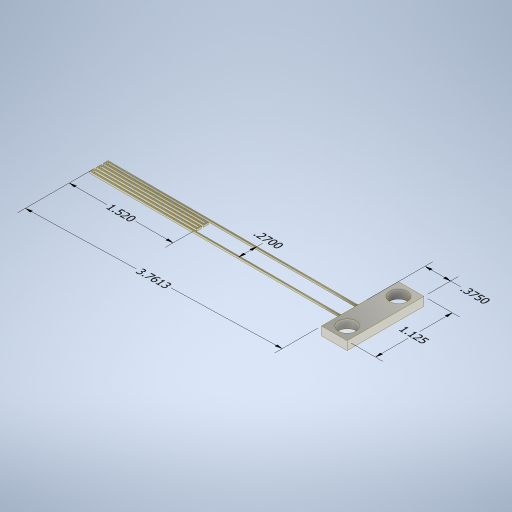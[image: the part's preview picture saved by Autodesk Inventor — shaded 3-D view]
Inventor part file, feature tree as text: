
AUTODESK INVENTOR PART (.ipt)
format: ipt  version: 2024.2 (Build 282272000, 272)  size: 348,160 bytes
history: native  units: in
note: dims shown in document units (in); Inventor stores cm internally (conversion verified against a paired STEP export)
features: other x6, sketch x4, plane x2, extrude x2, fillet x2, sweep x1
ambient origin geometry x8: Origin, YZ Plane, XZ Plane, XY Plane, X Axis, Y Axis, Z Axis, Center Point
bodies: Solid1 (feature_tree)
feature tree (17):
  other  "Annotations"
  sweep  "Sweep1"
  plane  "Work Plane1"
  plane  "Work Plane2"
  extrude  "Extrusion4"  Depth=0.05in
  fillet  "Fillet1"  Radius=0.05in
  extrude  "Extrusion5"  TaperAngle=0.0deg  [1 undecoded]
  fillet  "Fillet2"  Radius=0.05in
  sketch  "Sketch1"  dims[d0=3.75in d1=0.05in]
  sketch  "Sketch2"  dims[d2=1.5in d3=0.05in d4=0.05in]
  sketch  "Sketch6"  dims[d5=0.05in d6=0.0in d7=0.0in]
  sketch  "Sketch7"  dims[d11=0.25in d19=-0.25in d22=1.5in d23=0.05in d24=0.025in d25=1.125in d26=0.375in d28=0.1875in d29=0.0in d30=0.125in d31=0.0in d32=0.125in d33=0.26in d34=0.26in d35=0.75in d36=0.1875in d37=0.125in d38=0.0in d39=0.185in d40=0.185in d41=0.125in d42=0.2341in d43=0.169in d44=0.27in d45=0.2391in d46=0.1704in d47=3.7613in d48=0.2141in d49=0.2512in d50=1.52in d51=0.1604in d52=0.1602in d53=0.375in d54=0.248in d55=0.2288in d56=1.125in]
  other  "Linear Dimension 1"
  other  "Linear Dimension 2"
  other  "Linear Dimension 3"
  other  "Linear Dimension 4"
  other  "Linear Dimension 5"
note: 1 required parameter value undecoded (feature->parameter linkage not recoverable at this tier; creation-order binding heuristic only, values carry confidence <= 0.55)
